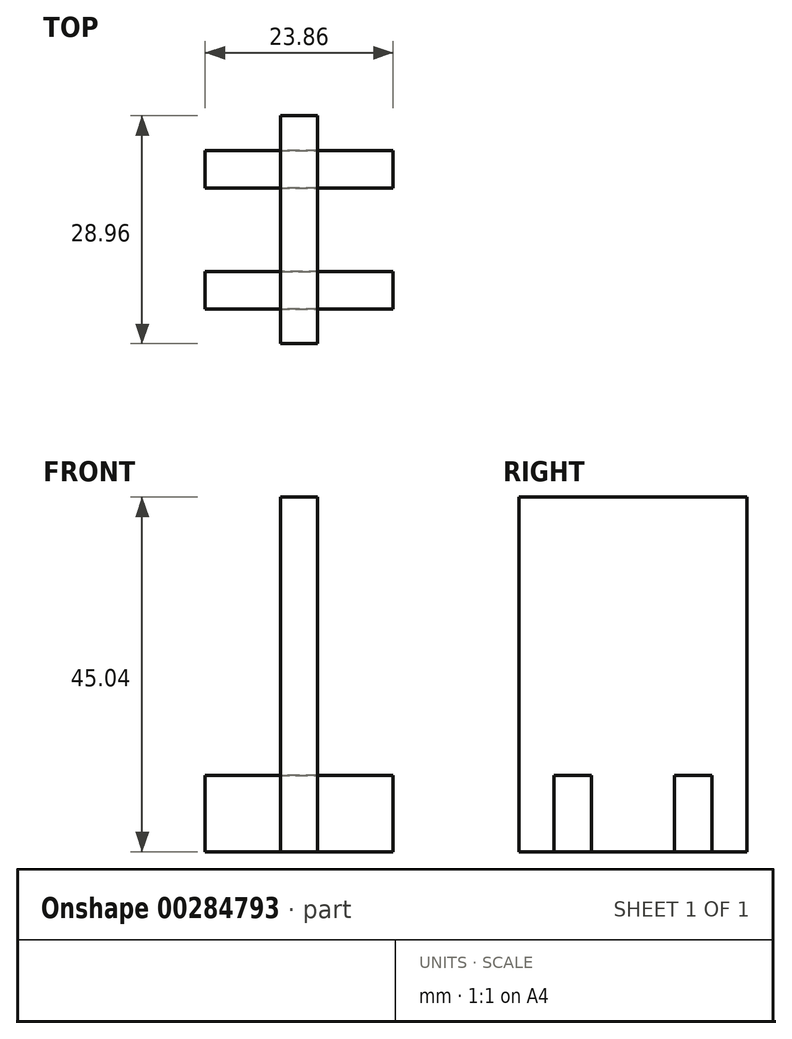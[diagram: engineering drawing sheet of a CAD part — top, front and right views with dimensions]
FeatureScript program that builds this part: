
annotation { "Feature Type Name" : "Feature", "Feature Type Description" : "" }
export const myFeature = defineFeature(function(context is Context, id is Id, definition is map)
    precondition{}
    {
        {
            var Q0;
            Q0=qCreatedBy(makeId("Right.planeOp"),FACE);
            var sketch = newSketch(context, id + "F0", { "sketchPlane" : qUnion([Q0])});
            skLineSegment(sketch, "E0.bottom", {"start": v(14.48, -22.52) * mm, "end": v(-14.48, -22.52) * mm});
            skLineSegment(sketch, "E0.top", {"start": v(14.48, 22.52) * mm, "end": v(-14.48, 22.52) * mm});
            skLineSegment(sketch, "E0.left", {"start": v(14.48, -22.52) * mm, "end": v(14.48, 22.52) * mm});
            skLineSegment(sketch, "E0.right", {"start": v(-14.48, -22.52) * mm, "end": v(-14.48, 22.52) * mm});
            skPoint(sketch, "E0.middle", {"position": v(0, 0) * mm});
            skLineSegment(sketch, "E1", {"start": v(-10.06, -22.52) * mm, "end": v(-10.06, -12.84) * mm});
            skLineSegment(sketch, "E2", {"start": v(-10.06, -12.84) * mm, "end": v(-5.28, -12.84) * mm});
            skLineSegment(sketch, "E3", {"start": v(-5.28, -12.84) * mm, "end": v(-5.28, -22.52) * mm});
            skLineSegment(sketch, "E4", {"start": v(0, 0) * mm, "end": v(0, -22.52) * mm, "construction": true});
            skLineSegment(sketch, "E5.MirrorCS", {"start": v(5.28, -12.84) * mm, "end": v(5.28, -22.52) * mm});
            skLineSegment(sketch, "E6.MirrorCS", {"start": v(10.06, -12.84) * mm, "end": v(5.28, -12.84) * mm});
            skLineSegment(sketch, "E7.MirrorCS", {"start": v(10.06, -22.52) * mm, "end": v(10.06, -12.84) * mm});
            skSolve(sketch);
        }
        {
            var Q0;
            Q0=makeQuery(id+"F0.imprint","IMPRINT",FACE,{"disambiguationData":[TD([[makeQuery(id+"F0.imprint","IMPRINT",EDGE,{"derivedFrom":sQuery(id+"F0.wireOp",EDGE,"E0.top")}),1.0]])]});
            extrude(context, id + "F1", {"entities" : qUnion([Q0]), "depth" : 4.7 * mm});
        }
        {
            var Q0;
            {var subQ0=sQuery(id+"F0.wireOp",EDGE,"E0.bottom");Q0=makeQuery(id+"F1.opExtrude","SWEPT_FACE",FACE,{"disambiguationData":[OSD([subQ0]),TDD([makeQuery(id+"F0.imprint","IMPRINT",EDGE,{"disambiguationData":[TD([[makeQuery(id+"F0.imprint","INTERSECT",VERTEX,{"derivedFrom":[subQ0,sQuery(id+"F0.wireOp",EDGE,"E3")]}),1.0]])],"derivedFrom":subQ0})])]});}
            var sketch = newSketch(context, id + "F2", { "sketchPlane" : qUnion([Q0])});
            skLineSegment(sketch, "E8.0.0", {"start": v(0, -5.28) * mm, "end": v(0, -10.06) * mm});
            skLineSegment(sketch, "E8.0.1", {"start": v(0, -10.06) * mm, "end": v(4.7, -10.06) * mm});
            skLineSegment(sketch, "E8.0.2", {"start": v(4.7, -10.06) * mm, "end": v(4.7, -5.28) * mm});
            skLineSegment(sketch, "E8.0.3", {"start": v(4.7, -5.28) * mm, "end": v(0, -5.28) * mm});
            skLineSegment(sketch, "E9", {"start": v(4.7, 0) * mm, "end": v(0, 0) * mm, "construction": true});
            skLineSegment(sketch, "E10.MirrorCS", {"start": v(4.7, 5.28) * mm, "end": v(0, 5.28) * mm});
            skLineSegment(sketch, "E11.MirrorCS", {"start": v(0, 5.28) * mm, "end": v(0, 10.06) * mm});
            skLineSegment(sketch, "E12.MirrorCS", {"start": v(4.7, 10.06) * mm, "end": v(4.7, 5.28) * mm});
            skLineSegment(sketch, "E13.MirrorCS", {"start": v(0, 10.06) * mm, "end": v(4.7, 10.06) * mm});
            skSolve(sketch);
        }
        {
            var Q0;
            Q0=makeQuery(id+"F2.imprint","IMPRINT",FACE,{"disambiguationData":[TD([[makeQuery(id+"F2.imprint","IMPRINT",EDGE,{"derivedFrom":sQuery(id+"F2.wireOp",EDGE,"E8.0.3")}),-1.0]])]});
            var sketch = newSketch(context, id + "F3", { "sketchPlane" : qUnion([Q0])});
            skLineSegment(sketch, "E14.0.0", {"start": v(0, -10.06) * mm, "end": v(4.7, -10.06) * mm});
            skLineSegment(sketch, "E14.0.1", {"start": v(4.7, -10.06) * mm, "end": v(4.7, -5.28) * mm});
            skLineSegment(sketch, "E14.0.2", {"start": v(4.7, -5.28) * mm, "end": v(0, -5.28) * mm});
            skLineSegment(sketch, "E14.0.3", {"start": v(0, -5.28) * mm, "end": v(0, -10.06) * mm});
            skLineSegment(sketch, "E15", {"start": v(2.35, -10.06) * mm, "end": v(2.35, -5.28) * mm, "construction": true});
            skPoint(sketch, "E16", {"position": v(2.35, -7.67) * mm});
            skLineSegment(sketch, "E17.bottom", {"start": v(-9.58, -5.28) * mm, "end": v(14.28, -5.28) * mm});
            skLineSegment(sketch, "E17.top", {"start": v(-9.58, -10.06) * mm, "end": v(14.28, -10.06) * mm});
            skLineSegment(sketch, "E17.left", {"start": v(-9.58, -5.28) * mm, "end": v(-9.58, -10.06) * mm});
            skLineSegment(sketch, "E17.right", {"start": v(14.28, -5.28) * mm, "end": v(14.28, -10.06) * mm});
            skLineSegment(sketch, "E18.MirrorCS", {"start": v(-9.58, 5.28) * mm, "end": v(14.28, 5.28) * mm});
            skLineSegment(sketch, "E19.MirrorCS", {"start": v(-9.58, 5.28) * mm, "end": v(-9.58, 10.06) * mm});
            skLineSegment(sketch, "E20.MirrorCS", {"start": v(-9.58, 10.06) * mm, "end": v(14.28, 10.06) * mm});
            skLineSegment(sketch, "E21.MirrorCS", {"start": v(14.28, 5.28) * mm, "end": v(14.28, 10.06) * mm});
            skSolve(sketch);
        }
        {
            var Q0;
            {var subQ0=sQuery(id+"F3.wireOp",EDGE,"E14.0.1");Q0=makeQuery(id+"F3.imprint","IMPRINT",FACE,{"disambiguationData":[TD([[makeQuery(id+"F3.imprint","IMPRINT",EDGE,{"derivedFrom":subQ0}),-1.0]])]});}
            var Q1;
            {var subQ0=sQuery(id+"F3.wireOp",EDGE,"E14.0.1");Q1=makeQuery(id+"F3.imprint","IMPRINT",FACE,{"disambiguationData":[TD([[makeQuery(id+"F3.imprint","IMPRINT",EDGE,{"derivedFrom":subQ0}),1.0]])]});}
            var Q2;
            {var subQ0=sQuery(id+"F3.wireOp",EDGE,"E14.0.3");Q2=makeQuery(id+"F3.imprint","IMPRINT",FACE,{"disambiguationData":[TD([[makeQuery(id+"F3.imprint","IMPRINT",EDGE,{"derivedFrom":subQ0}),-1.0]])]});}
            var Q3;
            Q3=makeQuery(id+"F2.imprint","IMPRINT",FACE,{"disambiguationData":[TD([[makeQuery(id+"F2.imprint","IMPRINT",EDGE,{"derivedFrom":sQuery(id+"F2.wireOp",EDGE,"E10.MirrorCS")}),-1.0]])]});
            var Q4;
            {var subQ0=sQuery(id+"F3.wireOp",EDGE,"E19.MirrorCS");Q4=makeQuery(id+"F3.imprint","IMPRINT",FACE,{"disambiguationData":[TD([[makeQuery(id+"F3.imprint","IMPRINT",EDGE,{"derivedFrom":subQ0}),-1.0]])]});}
            var Q5;
            Q5=makeQuery(id+"F1.opExtrude","SWEPT_FACE",FACE,{"disambiguationData":[OSD([sQuery(id+"F0.wireOp",EDGE,"E6.MirrorCS")])]});
            extrude(context, id + "F4", {"entities" : qUnion([Q0, Q1, Q2, Q3, Q4]), "endBound" : BoundingType.UP_TO_SURFACE, "oppositeDirection" : true, "endBoundEntityFace" : qUnion([Q5]), "depth" : 25 * mm});
        }
    });
